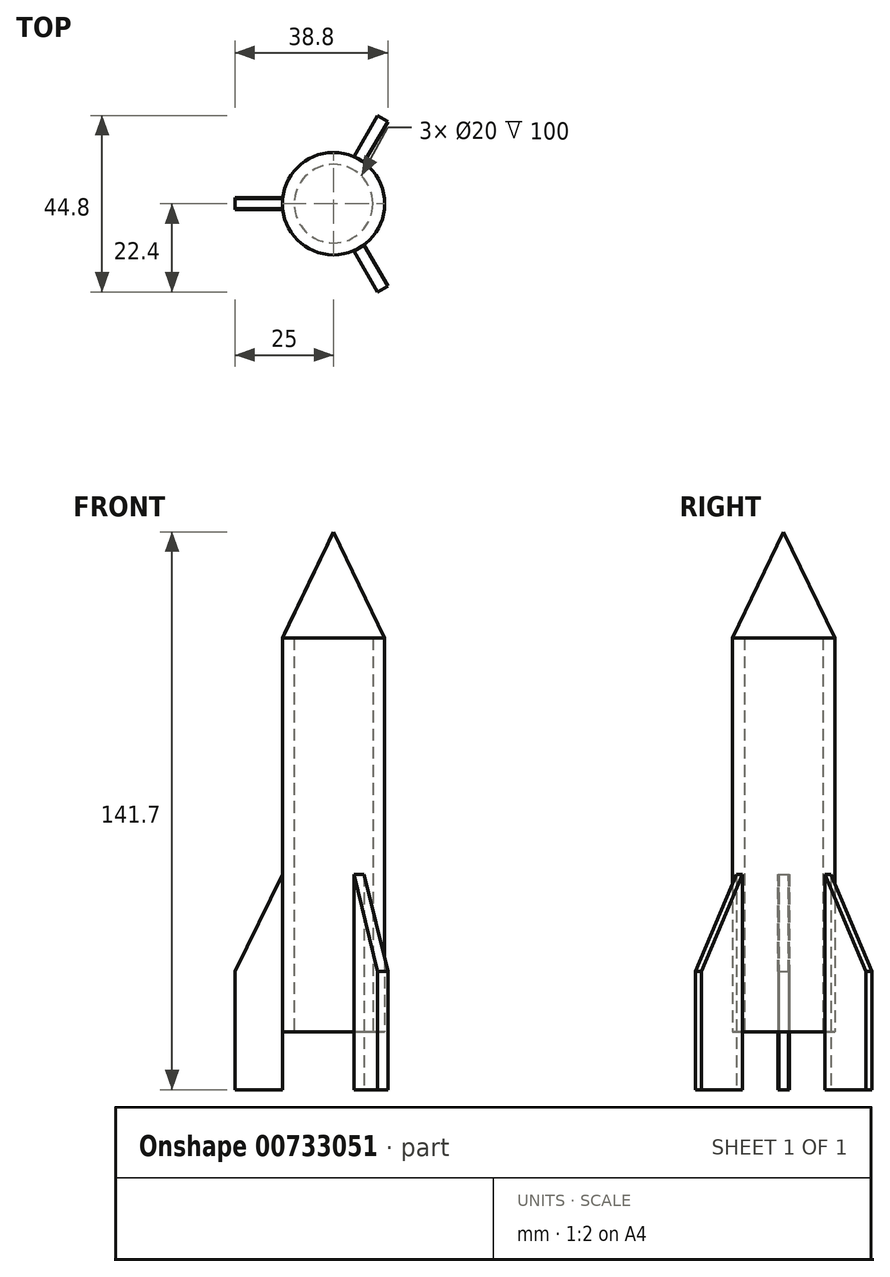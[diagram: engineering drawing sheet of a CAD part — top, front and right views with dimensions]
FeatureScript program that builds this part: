
annotation { "Feature Type Name" : "Feature", "Feature Type Description" : "" }
export const myFeature = defineFeature(function(context is Context, id is Id, definition is map)
    precondition{}
    {
        {
            var Q0;
            Q0=qCreatedBy(makeId("Front.planeOp"),FACE);
            var sketch = newSketch(context, id + "F0", { "sketchPlane" : qUnion([Q0])});
            skLineSegment(sketch, "E0", {"start": v(0, 0) * mm, "end": v(0, 127) * mm});
            skLineSegment(sketch, "E1", {"start": v(0, 127) * mm, "end": v(-13, 100.06) * mm});
            skLineSegment(sketch, "E2", {"start": v(-13, 100.06) * mm, "end": v(-13, 0) * mm});
            skLineSegment(sketch, "E3", {"start": v(-13, 0) * mm, "end": v(-10, 0) * mm});
            skLineSegment(sketch, "E4", {"start": v(-10, 0) * mm, "end": v(-10, 100) * mm});
            skLineSegment(sketch, "E5", {"start": v(-10, 100) * mm, "end": v(0, 100) * mm});
            skSolve(sketch);
        }
        {
            var Q0;
            Q0 = qSketchRegion(id + "F0", true);
            var Q1;
            Q1=sQuery(id+"F0.wireOp",EDGE,"E0");
            revolve(context, id + "F1", {"surfaceOperationType" : NewSurfaceOperationType.NEW, "entities" : qUnion([Q0]), "axis" : qUnion([Q1]), "revolveType" : RevolveType.FULL});
        }
        {
            var Q0;
            Q0=qCreatedBy(makeId("Front.planeOp"),FACE);
            var sketch = newSketch(context, id + "F2", { "sketchPlane" : qUnion([Q0])});
            skLineSegment(sketch, "E6", {"start": v(-25, 15.3) * mm, "end": v(-13, 40) * mm});
            skLineSegment(sketch, "E7", {"start": v(-13, -14.7) * mm, "end": v(-25, -14.7) * mm});
            skLineSegment(sketch, "E8", {"start": v(-25, 15.3) * mm, "end": v(-25, -14.7) * mm});
            skLineSegment(sketch, "E9", {"start": v(-13, -4.7) * mm, "end": v(-13, 95.3) * mm});
            skLineSegment(sketch, "E10", {"start": v(13, 100.06) * mm, "end": v(13, 0) * mm});
            skLineSegment(sketch, "E11", {"start": v(-13, -4.7) * mm, "end": v(-13, -14.7) * mm});
            skSolve(sketch);
        }
        {
            var Q0;
            Q0 = qSketchRegion(id + "F2", true);
            extrude(context, id + "F3", {"entities" : qUnion([Q0]), "operationType" : NewBodyOperationType.ADD, "endBound" : BoundingType.SYMMETRIC, "depth" : 3 * mm, "offsetDistance" : 25 * mm});
        }
        {
            var Q0;
            Q0=makeQuery(id+"F3.opExtrude","SWEPT_BODY",BODY,{"disambiguationData":[OSD([sQuery(id+"F2.wireOp",EDGE,"e22eb37e-d8dd-4329-a2d3-fbfdff4c98e4"),sQuery(id+"F2.wireOp",EDGE,"lLMWoRsq-RIhi-c7c5-fCH5-DzFpHTFsqkWn"),sQuery(id+"F2.wireOp",EDGE,"E6"),sQuery(id+"F2.wireOp",EDGE,"s4oJCqMo-VKWq-kCVp-h3GD-7KcSVkuLEeKC")])]});
            var Q1;
            Q1=makeQuery(id+"F1.opRevolve","SWEPT_BODY",BODY,{"disambiguationData":[OSD([sQuery(id+"F0.wireOp",EDGE,"E0"),sQuery(id+"F0.wireOp",EDGE,"E1"),sQuery(id+"F0.wireOp",EDGE,"E2"),sQuery(id+"F0.wireOp",EDGE,"E3"),sQuery(id+"F0.wireOp",EDGE,"E4"),sQuery(id+"F0.wireOp",EDGE,"E5")])]});
            var Q2;
            Q2=makeQuery(id+"F1.opRevolve","SWEPT_FACE",FACE,{"disambiguationData":[OSD([sQuery(id+"F0.wireOp",EDGE,"E2")])]});
            circularPattern(context, id + "F4", {"entities" : qUnion([Q0, Q1]), "axis" : qUnion([Q2]), "angle" : 360 * degree, "instanceCount" : 3, "equalSpace" : true});
        }
        {
            var Q0;
            Q0 = qSketchRegion(id + "F2", true);
            extrude(context, id + "F5", {"entities" : qUnion([Q0]), "endBound" : BoundingType.SYMMETRIC, "depth" : 2.5 * mm, "offsetDistance" : 25 * mm});
        }
    });
